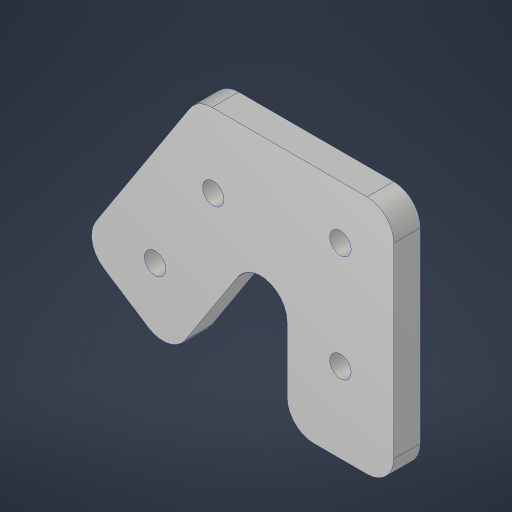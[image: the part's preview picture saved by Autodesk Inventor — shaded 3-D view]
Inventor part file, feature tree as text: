
AUTODESK INVENTOR PART (.ipt)
format: ipt  version: 2023.4 (Build 274418000, 418)  size: 205,312 bytes
history: native  units: in
note: dims shown in document units (in); Inventor stores cm internally (conversion verified against a paired STEP export)
features: sketch x1, extrude x1, hole x1, fillet x1
ambient origin geometry x8: Origin, YZ Plane, XZ Plane, XY Plane, X Axis, Y Axis, Z Axis, Center Point
bodies: Solid1 (feature_tree)
feature tree (4):
  sketch  "Sketch1"  dims[d0=1.0in d1=1.0in d2=0.2268in d3=2.0in d4=1.0in d5=0.5in d6=1.0in d7=0.5in d8=2.25in d9=0.25in d10=0.0in d11=0.201in d12=0.75in d13=0.385in d14=0.25in d15=0.5635in d16=1.0in d17=0.8108in d18=0.25in]
  extrude  "Extrusion1"  Depth=1.0in
  hole  "Hole1"  [1 undecoded]
  fillet  "Fillet1"  Radius=2.0in
note: 1 required parameter value undecoded (feature->parameter linkage not recoverable at this tier; creation-order binding heuristic only, values carry confidence <= 0.55)
